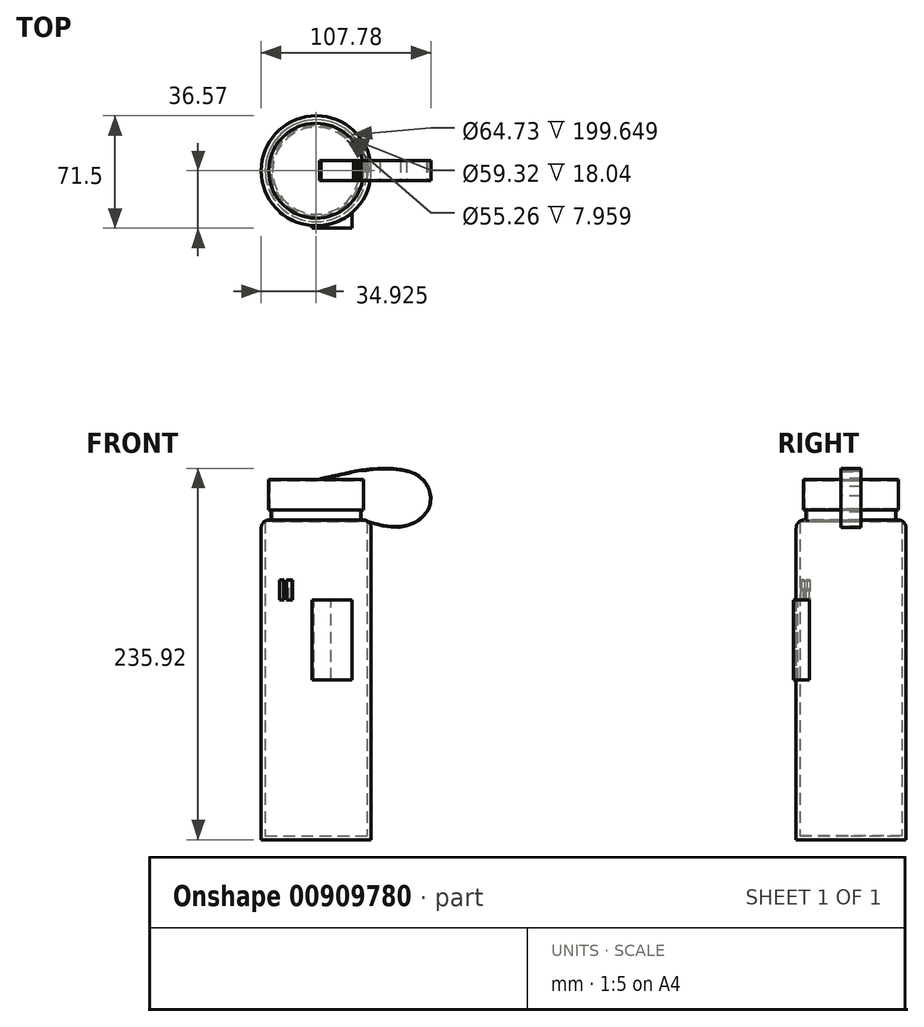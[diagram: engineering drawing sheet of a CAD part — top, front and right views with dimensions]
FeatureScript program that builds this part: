
annotation { "Feature Type Name" : "Feature", "Feature Type Description" : "" }
export const myFeature = defineFeature(function(context is Context, id is Id, definition is map)
    precondition{}
    {
        {
            var Q0;
            Q0=qCreatedBy(makeId("Front.planeOp"),FACE);
            var sketch = newSketch(context, id + "F0", { "sketchPlane" : qUnion([Q0])});
            skLineSegment(sketch, "E0", {"start": v(0, 0) * mm, "end": v(0, -203.2) * mm});
            skLineSegment(sketch, "E1", {"start": v(0, -203.2) * mm, "end": v(-34.92, -203.2) * mm});
            skLineSegment(sketch, "E2", {"start": v(-34.92, -203.2) * mm, "end": v(-34.92, -200.66) * mm});
            skLineSegment(sketch, "E3", {"start": v(0, -203.2) * mm, "end": v(-2.56, -203.2) * mm});
            skLineSegment(sketch, "E4", {"start": v(-34.92, -200.66) * mm, "end": v(-2.56, -200.66) * mm});
            skLineSegment(sketch, "E5", {"start": v(-2.56, -200.66) * mm, "end": v(-2.56, -2.35) * mm});
            skLineSegment(sketch, "E6", {"start": v(-6.35, 0) * mm, "end": v(0, 0) * mm});
            skLineSegment(sketch, "E7", {"start": v(-2.56, -2.35) * mm, "end": v(-2.56, -1.01) * mm});
            skLineSegment(sketch, "E8", {"start": v(-2.56, -1.01) * mm, "end": v(-7.3, -1.01) * mm});
            skLineSegment(sketch, "E9", {"start": v(-6.35, 0) * mm, "end": v(-6.35, 6.34) * mm});
            skLineSegment(sketch, "E10", {"start": v(-7.3, 6.34) * mm, "end": v(-7.3, -1.01) * mm});
            skLineSegment(sketch, "E11", {"start": v(-6.35, 6.34) * mm, "end": v(-4.76, 6.34) * mm});
            skLineSegment(sketch, "E12", {"start": v(-7.3, 6.34) * mm, "end": v(-7.3, 6.95) * mm});
            skLineSegment(sketch, "E13", {"start": v(-7.3, 6.95) * mm, "end": v(-5.27, 6.95) * mm});
            skLineSegment(sketch, "E14", {"start": v(-4.76, 6.34) * mm, "end": v(-4.76, 25.4) * mm});
            skLineSegment(sketch, "E15", {"start": v(-5.27, 6.95) * mm, "end": v(-5.27, 24.99) * mm});
            skLineSegment(sketch, "E16", {"start": v(-34.92, -203.2) * mm, "end": v(-34.92, 25.7) * mm, "construction": true});
            skLineSegment(sketch, "E17", {"start": v(-34.92, 25.7) * mm, "end": v(-4.76, 25.7) * mm});
            skLineSegment(sketch, "E18", {"start": v(-4.76, 25.7) * mm, "end": v(-4.76, 25.4) * mm});
            skLineSegment(sketch, "E19", {"start": v(-5.27, 24.99) * mm, "end": v(-34.92, 24.99) * mm});
            skLineSegment(sketch, "E20", {"start": v(-34.92, 25.7) * mm, "end": v(-34.92, 24.99) * mm});
            skSolve(sketch);
        }
        {
            var Q0;
            {var subQ0=sQuery(id+"F0.wireOp",EDGE,"E0");Q0=makeQuery(id+"F0.imprint","IMPRINT",FACE,{"disambiguationData":[TD([[makeQuery(id+"F0.imprint","IMPRINT",EDGE,{"derivedFrom":subQ0}),-1.0]])]});}
            var Q1;
            Q1=sQuery(id+"F0.wireOp",EDGE,"E16");
            revolve(context, id + "F1", {"surfaceOperationType" : NewSurfaceOperationType.NEW, "entities" : qUnion([Q0]), "axis" : qUnion([Q1]), "revolveType" : RevolveType.FULL});
        }
        {
            var Q0;
            Q0=makeQuery(id+"F1.opRevolve","SWEPT_EDGE",EDGE,{"disambiguationData":[OSD([sQuery(id+"F0.wireOp",EDGE,"E0"),sQuery(id+"F0.wireOp",EDGE,"E6")])]});
            fillet(context, id + "F2", {"entities" : qUnion([Q0]), "radius" : 5.08 * mm, "tangentPropagation" : true, "allowEdgeOverflow" : false});
        }
        {
            var Q0;
            Q0=qCreatedBy(makeId("Front.planeOp"),FACE);
            var sketch = newSketch(context, id + "F3", { "sketchPlane" : qUnion([Q0])});
            skFitSpline(sketch, "E21", {"points": [v(-31.93, 26.26) * mm, v(-18.22, 29.16) * mm, v(-2.39, 32.06) * mm, v(22.68, 31.27) * mm, v(35.34, 22.56) * mm, v(36.66, 7) * mm, v(20.3, -4.35) * mm, v(-6.07, 0) * mm], "startDerivative": vector(111.4, 23.07) * mm, "endDerivative": vector(-158.6, 50.58) * mm});
            skLineSegment(sketch, "E22", {"start": v(-6.07, 0) * mm, "end": v(-6, 0.09) * mm});
            skFitSpline(sketch, "E23", {"points": [v(-6, 0.09) * mm, v(3.15, -2.52) * mm, v(11.9, -4.19) * mm, v(18.79, -4.2) * mm], "startDerivative": vector(25.68, -7.7) * mm, "endDerivative": vector(22.15, 0.97) * mm});
            skFitSpline(sketch, "E24", {"points": [v(18.79, -4.2) * mm, v(24.61, -2.84) * mm, v(30.77, 0.44) * mm, v(35.07, 4.93) * mm], "startDerivative": vector(17.84, 3.2) * mm, "endDerivative": vector(11.9, 14.42) * mm});
            skFitSpline(sketch, "E25", {"points": [v(35.07, 4.93) * mm, v(36.8, 8.11) * mm, v(37.62, 13.27) * mm, v(37.48, 15.24) * mm], "startDerivative": vector(5.63, 8.18) * mm, "endDerivative": vector(-0.92, 6.66) * mm});
            skFitSpline(sketch, "E26", {"points": [v(37.48, 15.24) * mm, v(37.1, 17.6) * mm, v(36.32, 19.98) * mm, v(35.87, 21.06) * mm], "startDerivative": vector(-0.72, 6.3) * mm, "endDerivative": vector(-1.62, 3.74) * mm});
            skFitSpline(sketch, "E27", {"points": [v(35.87, 21.06) * mm, v(34.62, 23.08) * mm, v(33.23, 24.94) * mm, v(30.66, 27.27) * mm, v(26.44, 29.74) * mm, v(22.34, 31.04) * mm], "startDerivative": vector(-7.42, 12.34) * mm, "endDerivative": vector(-18.12, 4.71) * mm});
            skFitSpline(sketch, "E28", {"points": [v(22.34, 31.04) * mm, v(18.79, 31.78) * mm, v(13.3, 32.34) * mm, v(7.4, 32.4) * mm, v(5.68, 32.34) * mm], "startDerivative": vector(-14.22, 3.31) * mm, "endDerivative": vector(-8.77, -0.37) * mm});
            skFitSpline(sketch, "E29", {"points": [v(5.68, 32.34) * mm, v(1.65, 32.2) * mm, v(-1.17, 31.86) * mm, v(-3.7, 31.48) * mm, v(-5.43, 31.67) * mm], "startDerivative": vector(-13.87, -0.19) * mm, "endDerivative": vector(-8.09, -0.51) * mm});
            skFitSpline(sketch, "E30", {"points": [v(-4.09, 31.52) * mm, v(-6.39, 31.52) * mm, v(-8.75, 31.13) * mm, v(-11.19, 30.67) * mm, v(-13.29, 29.89) * mm, v(-15.07, 29.51) * mm, v(-17.64, 29) * mm, v(-21.34, 28.24) * mm, v(-23.44, 27.76) * mm, v(-27.01, 26.98) * mm, v(-31.56, 25.97) * mm, v(-32.19, 25.72) * mm], "startDerivative": vector(-25.82, -3.66) * mm, "endDerivative": vector(-9.6, -4.92) * mm});
            skLineSegment(sketch, "E31", {"start": v(-31.93, 26.26) * mm, "end": v(-32.5, 25.92) * mm});
            skLineSegment(sketch, "E32", {"start": v(-32.5, 25.92) * mm, "end": v(-32.74, 25.73) * mm});
            skLineSegment(sketch, "E33", {"start": v(-32.74, 25.73) * mm, "end": v(-32.19, 25.72) * mm});
            skSolve(sketch);
        }
        {
            var Q0;
            Q0 = qSketchRegion(id + "F3", true);
            extrude(context, id + "F4", {"entities" : qUnion([Q0]), "operationType" : NewBodyOperationType.ADD, "endBound" : BoundingType.SYMMETRIC, "oppositeDirection" : true, "depth" : 12.7 * mm, "offsetDistance" : 25.4 * mm});
        }
        {
            var Q0;
            Q0=qCreatedBy(makeId("Top.planeOp"),FACE);
            var sketch = newSketch(context, id + "F5", { "sketchPlane" : qUnion([Q0])});
            skFitSpline(sketch, "E34", {"points": [v(-25.45, -33.66) * mm, v(-20.58, -31.95) * mm, v(-15.1, -29.04) * mm, v(-12.19, -26.56) * mm], "startDerivative": vector(13.98, 4.39) * mm, "endDerivative": vector(8.84, 8.51) * mm});
            skLineSegment(sketch, "E35", {"start": v(-12.19, -26.56) * mm, "end": v(-12.19, -36.57) * mm});
            skLineSegment(sketch, "E36", {"start": v(-25.45, -36.57) * mm, "end": v(-12.19, -36.57) * mm});
            skFitSpline(sketch, "E37", {"points": [v(-25.45, -33.66) * mm, v(-31.28, -35.01) * mm, v(-36.42, -34.93) * mm], "startDerivative": vector(-11.37, -3.33) * mm, "endDerivative": vector(-10.54, 0.85) * mm});
            skLineSegment(sketch, "E38", {"start": v(-25.45, -36.57) * mm, "end": v(-37.51, -36.57) * mm});
            skLineSegment(sketch, "E39", {"start": v(-37.51, -36.57) * mm, "end": v(-37.51, -34.94) * mm});
            skLineSegment(sketch, "E40", {"start": v(-37.51, -34.94) * mm, "end": v(-36.42, -34.93) * mm});
            skFitSpline(sketch, "E41", {"points": [v(-53.5, -29.74) * mm, v(-53.39, -29.63) * mm], "startDerivative": vector(0.11, 0.1) * mm, "endDerivative": vector(0.11, 0.1) * mm});
            skFitSpline(sketch, "E42", {"points": [v(-53.39, -29.63) * mm, v(-52.85, -29.97) * mm, v(-52.32, -30.29) * mm, v(-51.54, -30.68) * mm, v(-50.44, -31.28) * mm, v(-49.9, -31.54) * mm], "startDerivative": vector(3, -1.9) * mm, "endDerivative": vector(2.73, -1.24) * mm});
            skFitSpline(sketch, "E43", {"points": [v(-55.46, -28.22) * mm, v(-56, -27.83) * mm, v(-56.6, -27.36) * mm, v(-57.26, -26.83) * mm, v(-57.99, -26.18) * mm], "startDerivative": vector(-2.35, 1.65) * mm, "endDerivative": vector(-2.67, 2.4) * mm});
            skLineSegment(sketch, "E44", {"start": v(-57.99, -26.18) * mm, "end": v(-58.19, -26.54) * mm});
            skLineSegment(sketch, "E45", {"start": v(-55.46, -28.22) * mm, "end": v(-55.82, -28.43) * mm});
            skLineSegment(sketch, "E46", {"start": v(-55.82, -28.43) * mm, "end": v(-58.19, -26.54) * mm});
            skLineSegment(sketch, "E47", {"start": v(-53.5, -29.74) * mm, "end": v(-53.63, -29.9) * mm});
            skLineSegment(sketch, "E48", {"start": v(-53.63, -29.9) * mm, "end": v(-50.22, -31.74) * mm});
            skLineSegment(sketch, "E49", {"start": v(-50.22, -31.74) * mm, "end": v(-49.9, -31.54) * mm});
            skSolve(sketch);
        }
        {
            var Q0;
            Q0=makeQuery(id+"F5.imprint","IMPRINT",FACE,{"disambiguationData":[TD([[makeQuery(id+"F5.imprint","IMPRINT",EDGE,{"derivedFrom":sQuery(id+"F5.wireOp",EDGE,"E34")}),-1.0]])]});
            extrude(context, id + "F6", {"entities" : qUnion([Q0]), "operationType" : NewBodyOperationType.ADD, "oppositeDirection" : true, "depth" : 101.6 * mm, "offsetDistance" : 25.4 * mm, "hasSecondDirection" : true, "secondDirectionOppositeDirection" : true, "secondDirectionDepth" : 50.8 * mm});
        }
        {
            var Q0;
            Q0=makeQuery(id+"F5.imprint","IMPRINT",FACE,{"disambiguationData":[TD([[makeQuery(id+"F5.imprint","IMPRINT",EDGE,{"derivedFrom":sQuery(id+"F5.wireOp",EDGE,"E43")}),1.0]])]});
            extrude(context, id + "F7", {"entities" : qUnion([Q0]), "operationType" : NewBodyOperationType.ADD, "oppositeDirection" : true, "depth" : 50.8 * mm, "offsetDistance" : 25.4 * mm, "hasSecondDirection" : true, "secondDirectionOppositeDirection" : true, "secondDirectionDepth" : 38.1 * mm});
        }
        {
            var Q0;
            Q0=makeQuery(id+"F5.imprint","IMPRINT",FACE,{"disambiguationData":[TD([[makeQuery(id+"F5.imprint","IMPRINT",EDGE,{"derivedFrom":sQuery(id+"F5.wireOp",EDGE,"E41")}),-1.0]])]});
            extrude(context, id + "F8", {"entities" : qUnion([Q0]), "operationType" : NewBodyOperationType.ADD, "oppositeDirection" : true, "depth" : 50.8 * mm, "offsetDistance" : 25.4 * mm, "hasSecondDirection" : true, "secondDirectionOppositeDirection" : true, "secondDirectionDepth" : 38.1 * mm});
        }
    });
